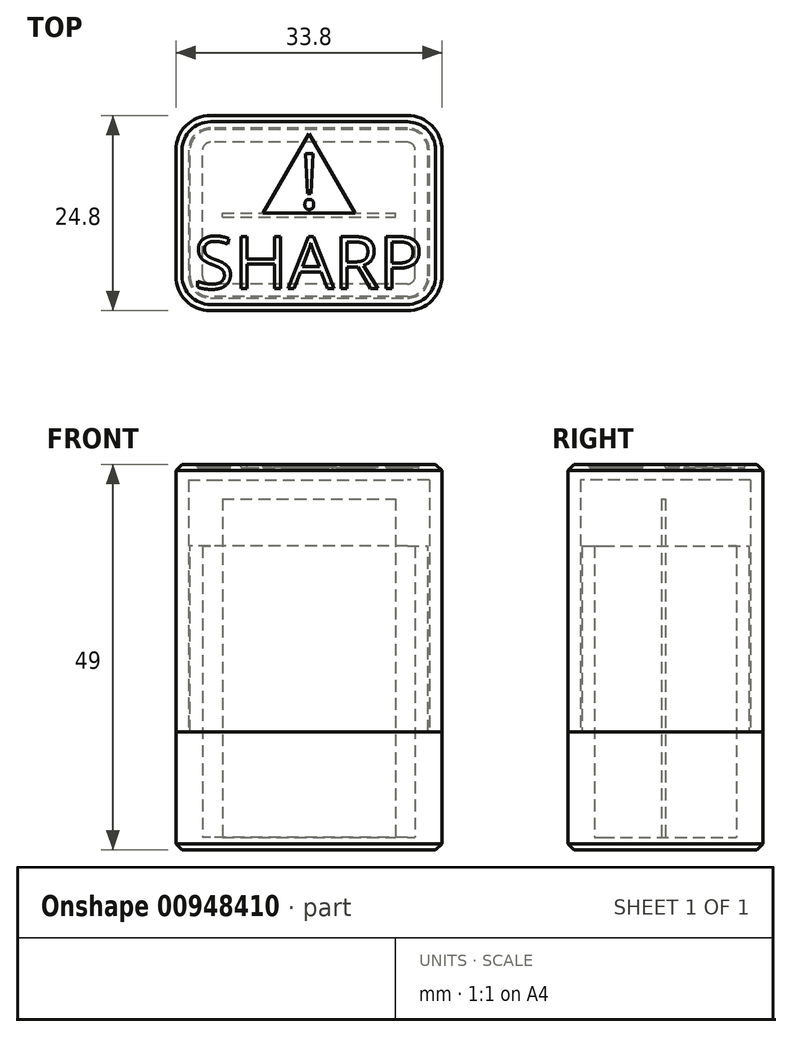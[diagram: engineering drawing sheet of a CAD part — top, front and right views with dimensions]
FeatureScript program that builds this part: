
annotation { "Feature Type Name" : "Feature", "Feature Type Description" : "" }
export const myFeature = defineFeature(function(context is Context, id is Id, definition is map)
    precondition{}
    {
        {
            assignVariable(context, id + "F0", {"name" : "WallThickness", "anyValue" : 1.6});
        }
        {
            var Q0;
            Q0=qCreatedBy(makeId("Front.planeOp"),FACE);
            var sketch = newSketch(context, id + "F1", { "sketchPlane" : qUnion([Q0])});
            skLineSegment(sketch, "E0", {"start": v(-11, 43) * mm, "end": v(11, 43) * mm});
            skLineSegment(sketch, "E1", {"start": v(11, 43) * mm, "end": v(11, 0) * mm});
            skLineSegment(sketch, "E2", {"start": v(-11, 43) * mm, "end": v(-11, 0) * mm});
            skLineSegment(sketch, "E3", {"start": v(-11, 0) * mm, "end": v(11, 0) * mm});
            skSolve(sketch);
        }
        {
            var Q0;
            Q0=qSketchRegion(id+"F1",true);
            extrude(context, id + "F2", {"entities" : qUnion([Q0]), "depth" : .5 * mm, "offsetDistance" : 25 * mm});
        }
        {
            var Q0;
            Q0=qCreatedBy(makeId("Top.planeOp"),FACE);
            var sketch = newSketch(context, id + "F3", { "sketchPlane" : qUnion([Q0])});
            skLineSegment(sketch, "E4.bottom", {"start": v(12.5, -9) * mm, "end": v(-12.5, -9) * mm});
            skLineSegment(sketch, "E4.top", {"start": v(12.5, 9) * mm, "end": v(-12.5, 9) * mm});
            skLineSegment(sketch, "E4.left", {"start": v(13.5, -8) * mm, "end": v(13.5, 8) * mm});
            skLineSegment(sketch, "E4.right", {"start": v(-13.5, -8) * mm, "end": v(-13.5, 8) * mm});
            skPoint(sketch, "E4.middle", {"position": v(0, 0) * mm});
            skPoint(sketch, "E5.visualSharp", {"position": v(13.5, -9) * mm});
            skArc(sketch, "E5.filletArc", {"start": v(12.5, -9) * mm, "mid": v(13.2, -8.7) * mm, "end": v(13.5, -8) * mm});
            skPoint(sketch, "E6.visualSharp", {"position": v(13.5, 9) * mm});
            skArc(sketch, "E6.filletArc", {"start": v(13.5, 8) * mm, "mid": v(13.2, 8.7) * mm, "end": v(12.5, 9) * mm});
            skPoint(sketch, "E7.visualSharp", {"position": v(-13.5, -9) * mm});
            skArc(sketch, "E7.filletArc", {"start": v(-13.5, -8) * mm, "mid": v(-13.2, -8.7) * mm, "end": v(-12.5, -9) * mm});
            skPoint(sketch, "E8.visualSharp", {"position": v(-13.5, 9) * mm});
            skArc(sketch, "E8.filletArc", {"start": v(-12.5, 9) * mm, "mid": v(-13.2, 8.7) * mm, "end": v(-13.5, 8) * mm});
            skSolve(sketch);
        }
        {
            var Q0;
            Q0=makeQuery(id+"F3.imprint","IMPRINT",FACE,{"disambiguationData":[TD([[makeQuery(id+"F3.imprint","IMPRINT",EDGE,{"derivedFrom":sQuery(id+"F3.wireOp",EDGE,"E4.bottom")}),-1.0]])]});
            extrude(context, id + "F4", {"entities" : qUnion([Q0]), "depth" : 37 * mm, "offsetDistance" : 25 * mm});
        }
        {
            var Q0;
            Q0=makeQuery(id+"F4.opExtrude","CAP_FACE",FACE,{"disambiguationData":[OSD([sQuery(id+"F3.wireOp",EDGE,"E4.bottom"),sQuery(id+"F3.wireOp",EDGE,"E4.top"),sQuery(id+"F3.wireOp",EDGE,"E4.left"),sQuery(id+"F3.wireOp",EDGE,"E4.right")])],"isStart":false});
            shell(context, id + "F5", {"entities" : qUnion([Q0]), "thickness" : (getVariable(context, 'WallThickness')) * mm, "oppositeDirection" : true});
        }
        {
            var Q0;
            Q0=makeQuery(id+"F4.opExtrude","CAP_FACE",FACE,{"disambiguationData":[OSD([sQuery(id+"F3.wireOp",EDGE,"E4.bottom"),sQuery(id+"F3.wireOp",EDGE,"E4.top"),sQuery(id+"F3.wireOp",EDGE,"E4.left"),sQuery(id+"F3.wireOp",EDGE,"E4.right"),sQuery(id+"F3.wireOp",EDGE,"E5.filletArc"),sQuery(id+"F3.wireOp",EDGE,"E6.filletArc"),sQuery(id+"F3.wireOp",EDGE,"E7.filletArc"),sQuery(id+"F3.wireOp",EDGE,"E8.filletArc")])],"isStart":true});
            var sketch = newSketch(context, id + "F6", { "sketchPlane" : qUnion([Q0])});
            skPoint(sketch, "E9.0", {"position": v(-14.34, -9.84) * mm});
            skArc(sketch, "E10.0", {"start": v(-12.5, -10.6) * mm, "mid": v(-14.34, -9.84) * mm, "end": v(-15.1, -8) * mm});
            skLineSegment(sketch, "E11.0", {"start": v(12.5, -10.6) * mm, "end": v(-12.5, -10.6) * mm});
            skPoint(sketch, "E12.0", {"position": v(14.34, -9.84) * mm});
            skLineSegment(sketch, "E13.0", {"start": v(15.1, 8) * mm, "end": v(15.1, -8) * mm});
            skArc(sketch, "E14.0", {"start": v(12.5, 10.6) * mm, "mid": v(14.34, 9.84) * mm, "end": v(15.1, 8) * mm});
            skLineSegment(sketch, "E15.0", {"start": v(12.5, 10.6) * mm, "end": v(-12.5, 10.6) * mm});
            skArc(sketch, "E16.0", {"start": v(-15.1, 8) * mm, "mid": v(-14.34, 9.84) * mm, "end": v(-12.5, 10.6) * mm});
            skLineSegment(sketch, "E17.0", {"start": v(-15.1, 8) * mm, "end": v(-15.1, -8) * mm});
            skLineSegment(sketch, "E18.0", {"start": v(12.5, -12.4) * mm, "end": v(-12.5, -12.4) * mm});
            skArc(sketch, "E18.1", {"start": v(16.9, -8) * mm, "mid": v(15.61, -11.11) * mm, "end": v(12.5, -12.4) * mm});
            skArc(sketch, "E18.2", {"start": v(-12.5, -12.4) * mm, "mid": v(-15.61, -11.11) * mm, "end": v(-16.9, -8) * mm});
            skLineSegment(sketch, "E18.3", {"start": v(16.9, 8) * mm, "end": v(16.9, -8) * mm});
            skLineSegment(sketch, "E18.4", {"start": v(-16.9, 8) * mm, "end": v(-16.9, -8) * mm});
            skArc(sketch, "E18.5", {"start": v(-16.9, 8) * mm, "mid": v(-15.61, 11.11) * mm, "end": v(-12.5, 12.4) * mm});
            skLineSegment(sketch, "E18.6", {"start": v(12.5, 12.4) * mm, "end": v(-12.5, 12.4) * mm});
            skArc(sketch, "E18.7", {"start": v(12.5, 12.4) * mm, "mid": v(15.61, 11.11) * mm, "end": v(16.9, 8) * mm});
            skArc(sketch, "E19.0", {"start": v(15.1, -8) * mm, "mid": v(14.34, -9.84) * mm, "end": v(12.5, -10.6) * mm});
            skSolve(sketch);
        }
        {
            var Q0;
            Q0=qSketchRegion(id+"F6",true);
            extrude(context, id + "F7", {"entities" : qUnion([Q0]), "operationType" : NewBodyOperationType.ADD, "oppositeDirection" : true, "depth" : 15 * mm, "offsetDistance" : 25 * mm});
        }
        {
            var Q0;
            {var subQ0=sQuery(id+"F6.wireOp",EDGE,"E18.0");var subQ1=sQuery(id+"F6.wireOp",EDGE,"E18.1");var subQ2=sQuery(id+"F6.wireOp",EDGE,"E18.2");var subQ3=sQuery(id+"F6.wireOp",EDGE,"E18.3");var subQ4=sQuery(id+"F6.wireOp",EDGE,"E18.4");var subQ5=sQuery(id+"F6.wireOp",EDGE,"E18.5");var subQ6=sQuery(id+"F6.wireOp",EDGE,"E18.6");var subQ7=sQuery(id+"F6.wireOp",EDGE,"E18.7");Q0=makeQuery(id+"F7.boolean.opBoolean","SPLIT",FACE,{"disambiguationData":[TD([makeQuery(id+"F4.opExtrude","SWEPT_FACE",FACE,{"disambiguationData":[OSD([sQuery(id+"F3.wireOp",EDGE,"E4.bottom")])]})])],"derivedFrom":makeQuery(id+"F7.opExtrude","CAP_FACE",FACE,{"disambiguationData":[OSD([subQ0,subQ1,subQ2,subQ3,subQ4,subQ5,subQ6,subQ7])],"isStart":false})});}
            var sketch = newSketch(context, id + "F8", { "sketchPlane" : qUnion([Q0])});
            skArc(sketch, "E20.0.0", {"start": v(12.5, -12.4) * mm, "mid": v(15.61, -11.11) * mm, "end": v(16.9, -8) * mm});
            skLineSegment(sketch, "E20.0.1", {"start": v(16.9, -8) * mm, "end": v(16.9, 8) * mm});
            skArc(sketch, "E20.0.2", {"start": v(16.9, 8) * mm, "mid": v(15.61, 11.11) * mm, "end": v(12.5, 12.4) * mm});
            skLineSegment(sketch, "E20.0.3", {"start": v(12.5, 12.4) * mm, "end": v(-12.5, 12.4) * mm});
            skArc(sketch, "E20.0.4", {"start": v(-12.5, 12.4) * mm, "mid": v(-15.61, 11.11) * mm, "end": v(-16.9, 8) * mm});
            skLineSegment(sketch, "E20.0.5", {"start": v(-16.9, 8) * mm, "end": v(-16.9, -8) * mm});
            skArc(sketch, "E20.0.6", {"start": v(-16.9, -8) * mm, "mid": v(-15.61, -11.11) * mm, "end": v(-12.5, -12.4) * mm});
            skLineSegment(sketch, "E20.0.7", {"start": v(-12.5, -12.4) * mm, "end": v(12.5, -12.4) * mm});
            skLineSegment(sketch, "E21.0", {"start": v(-12.5, -10.8) * mm, "end": v(12.5, -10.8) * mm});
            skArc(sketch, "E21.1", {"start": v(-15.3, -8) * mm, "mid": v(-14.48, -9.98) * mm, "end": v(-12.5, -10.8) * mm});
            skArc(sketch, "E21.2", {"start": v(12.5, -10.8) * mm, "mid": v(14.48, -9.98) * mm, "end": v(15.3, -8) * mm});
            skLineSegment(sketch, "E21.3", {"start": v(-15.3, 8) * mm, "end": v(-15.3, -8) * mm});
            skLineSegment(sketch, "E21.4", {"start": v(15.3, -8) * mm, "end": v(15.3, 8) * mm});
            skArc(sketch, "E21.5", {"start": v(15.3, 8) * mm, "mid": v(14.48, 9.98) * mm, "end": v(12.5, 10.8) * mm});
            skLineSegment(sketch, "E21.6", {"start": v(12.5, 10.8) * mm, "end": v(-12.5, 10.8) * mm});
            skArc(sketch, "E21.7", {"start": v(-12.5, 10.8) * mm, "mid": v(-14.48, 9.98) * mm, "end": v(-15.3, 8) * mm});
            skSolve(sketch);
        }
        {
            var Q0;
            Q0=qSketchRegion(id+"F8",true);
            extrude(context, id + "F9", {"entities" : qUnion([Q0]), "depth" : 32 * mm, "offsetDistance" : 25 * mm});
        }
        {
            var Q0;
            Q0=makeQuery(id+"F9.opExtrude","CAP_FACE",FACE,{"disambiguationData":[OSD([sQuery(id+"F8.wireOp",EDGE,"E20.0.0"),sQuery(id+"F8.wireOp",EDGE,"E20.0.1"),sQuery(id+"F8.wireOp",EDGE,"E20.0.2"),sQuery(id+"F8.wireOp",EDGE,"E20.0.3"),sQuery(id+"F8.wireOp",EDGE,"E20.0.4"),sQuery(id+"F8.wireOp",EDGE,"E20.0.5"),sQuery(id+"F8.wireOp",EDGE,"E20.0.6"),sQuery(id+"F8.wireOp",EDGE,"E20.0.7"),sQuery(id+"F8.wireOp",EDGE,"E21.0"),sQuery(id+"F8.wireOp",EDGE,"E21.1"),sQuery(id+"F8.wireOp",EDGE,"E21.2"),sQuery(id+"F8.wireOp",EDGE,"E21.3"),sQuery(id+"F8.wireOp",EDGE,"E21.4"),sQuery(id+"F8.wireOp",EDGE,"E21.5"),sQuery(id+"F8.wireOp",EDGE,"E21.6"),sQuery(id+"F8.wireOp",EDGE,"E21.7")])],"isStart":false});
            var sketch = newSketch(context, id + "F10", { "sketchPlane" : qUnion([Q0])});
            skLineSegment(sketch, "E22.0.0", {"start": v(-12.5, -12.4) * mm, "end": v(12.5, -12.4) * mm});
            skArc(sketch, "E22.0.1", {"start": v(12.5, -12.4) * mm, "mid": v(15.61, -11.11) * mm, "end": v(16.9, -8) * mm});
            skLineSegment(sketch, "E22.0.2", {"start": v(16.9, -8) * mm, "end": v(16.9, 8) * mm});
            skArc(sketch, "E22.0.3", {"start": v(16.9, 8) * mm, "mid": v(15.61, 11.11) * mm, "end": v(12.5, 12.4) * mm});
            skLineSegment(sketch, "E22.0.4", {"start": v(12.5, 12.4) * mm, "end": v(-12.5, 12.4) * mm});
            skArc(sketch, "E22.0.5", {"start": v(-12.5, 12.4) * mm, "mid": v(-15.61, 11.11) * mm, "end": v(-16.9, 8) * mm});
            skLineSegment(sketch, "E22.0.6", {"start": v(-16.9, 8) * mm, "end": v(-16.9, -8) * mm});
            skArc(sketch, "E22.0.7", {"start": v(-16.9, -8) * mm, "mid": v(-15.61, -11.11) * mm, "end": v(-12.5, -12.4) * mm});
            skSolve(sketch);
        }
        {
            var Q0;
            Q0=qSketchRegion(id+"F10",true);
            extrude(context, id + "F11", {"entities" : qUnion([Q0]), "operationType" : NewBodyOperationType.ADD, "depth" : 2 * mm, "offsetDistance" : 25 * mm});
        }
        {
            var Q0;
            Q0=makeQuery(id+"F11.opExtrude","CAP_EDGE",EDGE,{"disambiguationData":[OSD([sQuery(id+"F10.wireOp",EDGE,"E22.0.2")])],"isStart":false});
            var Q1;
            Q1=makeQuery(id+"F7.opExtrude","CAP_EDGE",EDGE,{"disambiguationData":[OSD([sQuery(id+"F6.wireOp",EDGE,"E18.3")])],"isStart":true});
            chamfer(context, id + "F12", {"entities" : qUnion([Q0, Q1]), "width" : .8 * mm, "tangentPropagation" : true});
        }
        {
            var Q0;
            Q0=makeQuery(id+"F11.opExtrude","CAP_FACE",FACE,{"disambiguationData":[OSD([sQuery(id+"F10.wireOp",EDGE,"E22.0.0"),sQuery(id+"F10.wireOp",EDGE,"E22.0.1"),sQuery(id+"F10.wireOp",EDGE,"E22.0.2"),sQuery(id+"F10.wireOp",EDGE,"E22.0.3"),sQuery(id+"F10.wireOp",EDGE,"E22.0.4"),sQuery(id+"F10.wireOp",EDGE,"E22.0.5"),sQuery(id+"F10.wireOp",EDGE,"E22.0.6"),sQuery(id+"F10.wireOp",EDGE,"E22.0.7")])],"isStart":false});
            var sketch = newSketch(context, id + "F13", { "sketchPlane" : qUnion([Q0])});
            skText(sketch, "E23", { "text": "SHARP", "fontName": "OpenSans-Regular.ttf"});
            skLineSegment(sketch, "E24", {"start": v(0, 10.1) * mm, "end": v(-5.83, 0) * mm});
            skLineSegment(sketch, "E25", {"start": v(-5.83, 0) * mm, "end": v(5.83, 0) * mm});
            skLineSegment(sketch, "E26", {"start": v(5.83, 0) * mm, "end": v(0, 10.1) * mm});
            skText(sketch, "E27", { "text": "!", "fontName": "OpenSans-Regular.ttf"});
            const initialGuessF13  = {"E23": [-0.0146, -0.0096, 1, 0, 0.00667], "E27": [-0.00125, 0.0006, 1, 0, 0.00701]};
            skSetInitialGuess(sketch, initialGuessF13);
            skSolve(sketch);
        }
        {
            var Q0;
            Q0 = qSketchRegion(id + "F13", true);
            extrude(context, id + "F14", {"entities" : qUnion([Q0]), "operationType" : NewBodyOperationType.REMOVE, "oppositeDirection" : true, "depth" : 0.4 * mm, "offsetDistance" : 25 * mm});
        }
    });
